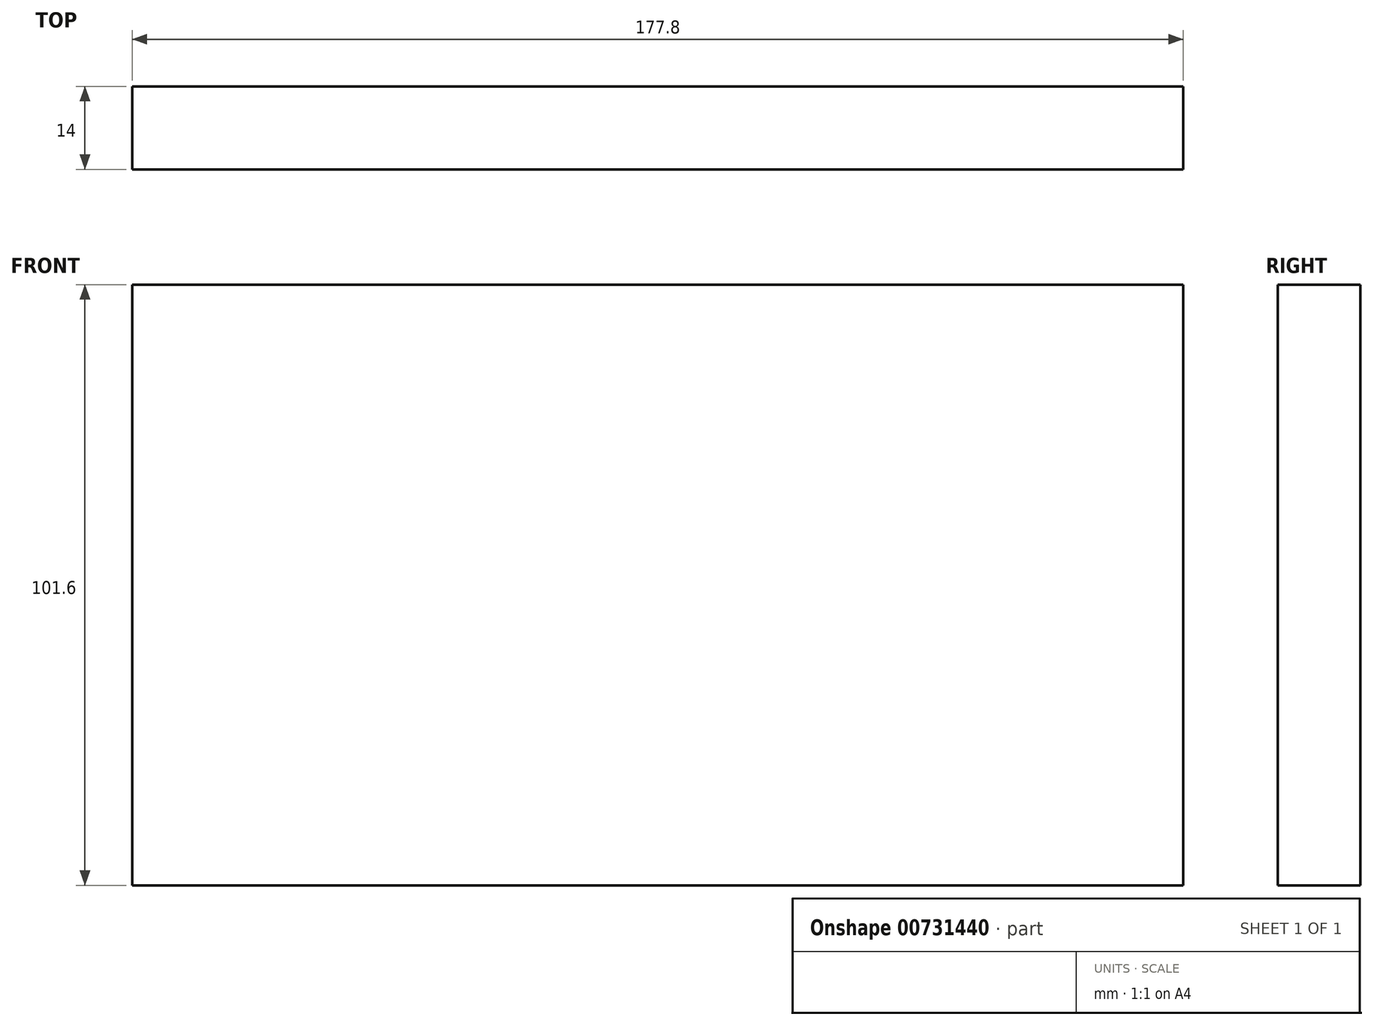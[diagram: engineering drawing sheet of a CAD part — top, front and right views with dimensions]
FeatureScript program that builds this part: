
annotation { "Feature Type Name" : "Feature", "Feature Type Description" : "" }
export const myFeature = defineFeature(function(context is Context, id is Id, definition is map)
    precondition{}
    {
        {
            var Q0;
            Q0=qCreatedBy(makeId("Front.planeOp"),FACE);
            var sketch = newSketch(context, id + "F0", { "sketchPlane" : qUnion([Q0])});
            skLineSegment(sketch, "E0.bottom", {"start": v(-88.9, 50.8) * mm, "end": v(88.9, 50.8) * mm});
            skLineSegment(sketch, "E0.top", {"start": v(-88.9, -50.8) * mm, "end": v(88.9, -50.8) * mm});
            skLineSegment(sketch, "E0.left", {"start": v(-88.9, 50.8) * mm, "end": v(-88.9, -50.8) * mm});
            skLineSegment(sketch, "E0.right", {"start": v(88.9, 50.8) * mm, "end": v(88.9, -50.8) * mm});
            skSolve(sketch);
        }
        {
            var Q0;
            Q0 = qSketchRegion(id + "F0", true);
            extrude(context, id + "F1", {"entities" : qUnion([Q0]), "depth" : 14 * mm, "offsetDistance" : 25 * mm});
        }
    });
